# Revit family: D2DTYP006
name_source: partatom
category: Furniture
units: mm (PartAtom-declared; Revit-internal decimal feet)

## family parameters
Always vertical = Yes
Cut with Voids When Loaded = No
OmniClass Number = 23.40.20.00
OmniClass Title = General Furniture and Specialties
Render Appearance Source = Family Geometry
Room Calculation Point = No
Shared = No
Work Plane-Based = No

## types (1)
- D2DTYP006
    Cost = 58870 $
    Default Elevation = 0 mm  [stored 0 ft]
    Description = 12 x Stow No Arms Mesh Back/fabric Choice Seat, 2 x SINGLE CIRCUIT INFEED 72", 6 x TABLE MODESTY 72"W, 6 x TBL, REC, 2mm, 24Dx72Wx29H, FLIP, CSTRP POWERED LINE 1, 3 x TBL, REC, 2mm, 30Dx72Wx29H, FLIP, CSTRP SINGLE CIRCUIT PWR
    Exported From CET Designer = Yes
    Manufacturer = AIS
    Model = 6820C
    Show D2DTYP006 = Yes
    VisibilityIndex = 0

note: [stored X ft] marks values corroborated as IEEE doubles in the binary element streams (Revit-internal decimal feet)

## geometry (parser evidence)
native form markers: Sweep x3
no freeform markers — native parametric forms only
